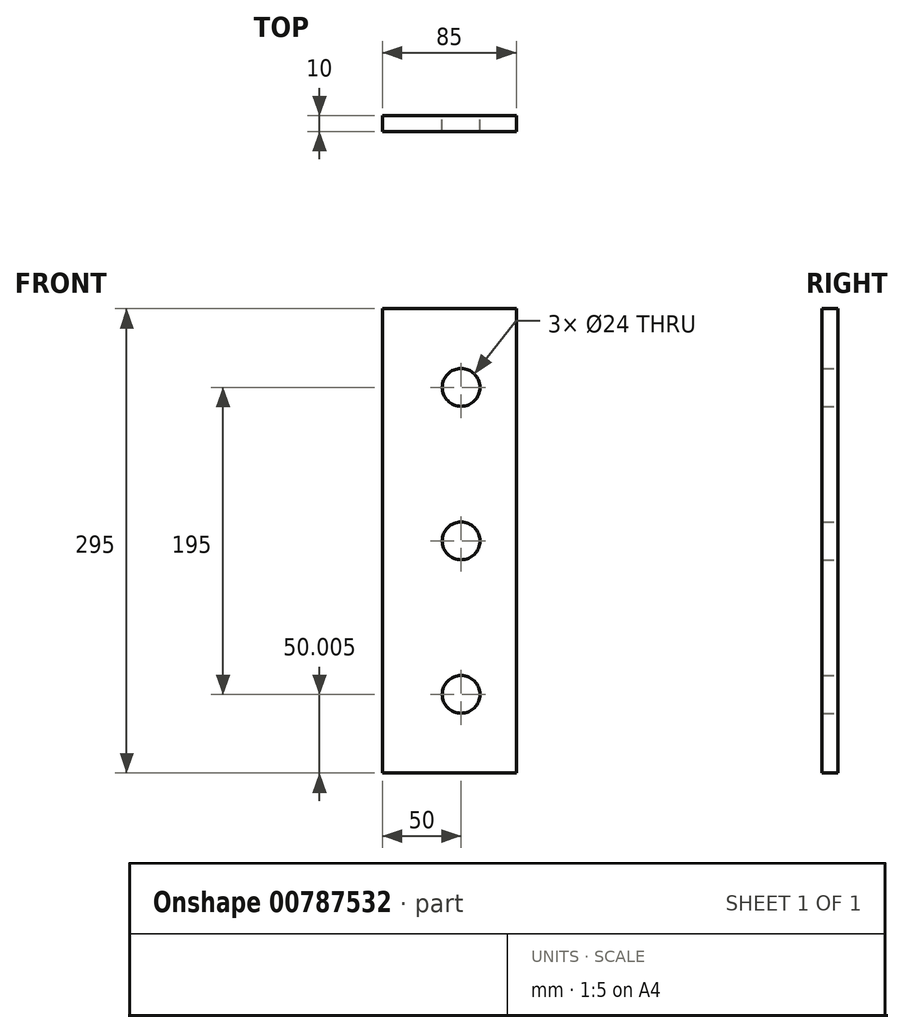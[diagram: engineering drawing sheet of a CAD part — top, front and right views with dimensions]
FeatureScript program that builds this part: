
annotation { "Feature Type Name" : "Feature", "Feature Type Description" : "" }
export const myFeature = defineFeature(function(context is Context, id is Id, definition is map)
    precondition{}
    {
        {
            var Q0;
            Q0=qCreatedBy(makeId("Front.planeOp"),FACE);
            var sketch = newSketch(context, id + "F0", { "sketchPlane" : qUnion([Q0])});
            skLineSegment(sketch, "E0.bottom", {"start": v(-37.42, 207.34) * mm, "end": v(47.58, 207.34) * mm});
            skLineSegment(sketch, "E0.top", {"start": v(-37.42, -87.66) * mm, "end": v(47.58, -87.66) * mm});
            skLineSegment(sketch, "E0.left", {"start": v(-37.42, 207.34) * mm, "end": v(-37.42, -87.66) * mm});
            skLineSegment(sketch, "E0.right", {"start": v(47.58, 207.34) * mm, "end": v(47.58, -87.66) * mm});
            skLineSegment(sketch, "E1", {"start": v(12.58, 207.34) * mm, "end": v(12.58, -87.66) * mm, "construction": true});
            skCircle(sketch, "E2", {"center": v(12.58, 157.34) * mm, "radius": 12 * mm});
            skCircle(sketch, "E3", {"center": v(12.58, 59.84) * mm, "radius": 12 * mm});
            skCircle(sketch, "E4", {"center": v(12.58, -37.66) * mm, "radius": 12 * mm});
            skSolve(sketch);
        }
        {
            var Q0;
            Q0 = qSketchRegion(id + "F0", true);
            extrude(context, id + "F1", {"entities" : qUnion([Q0]), "depth" : 10 * mm, "offsetDistance" : 25 * mm});
        }
    });
